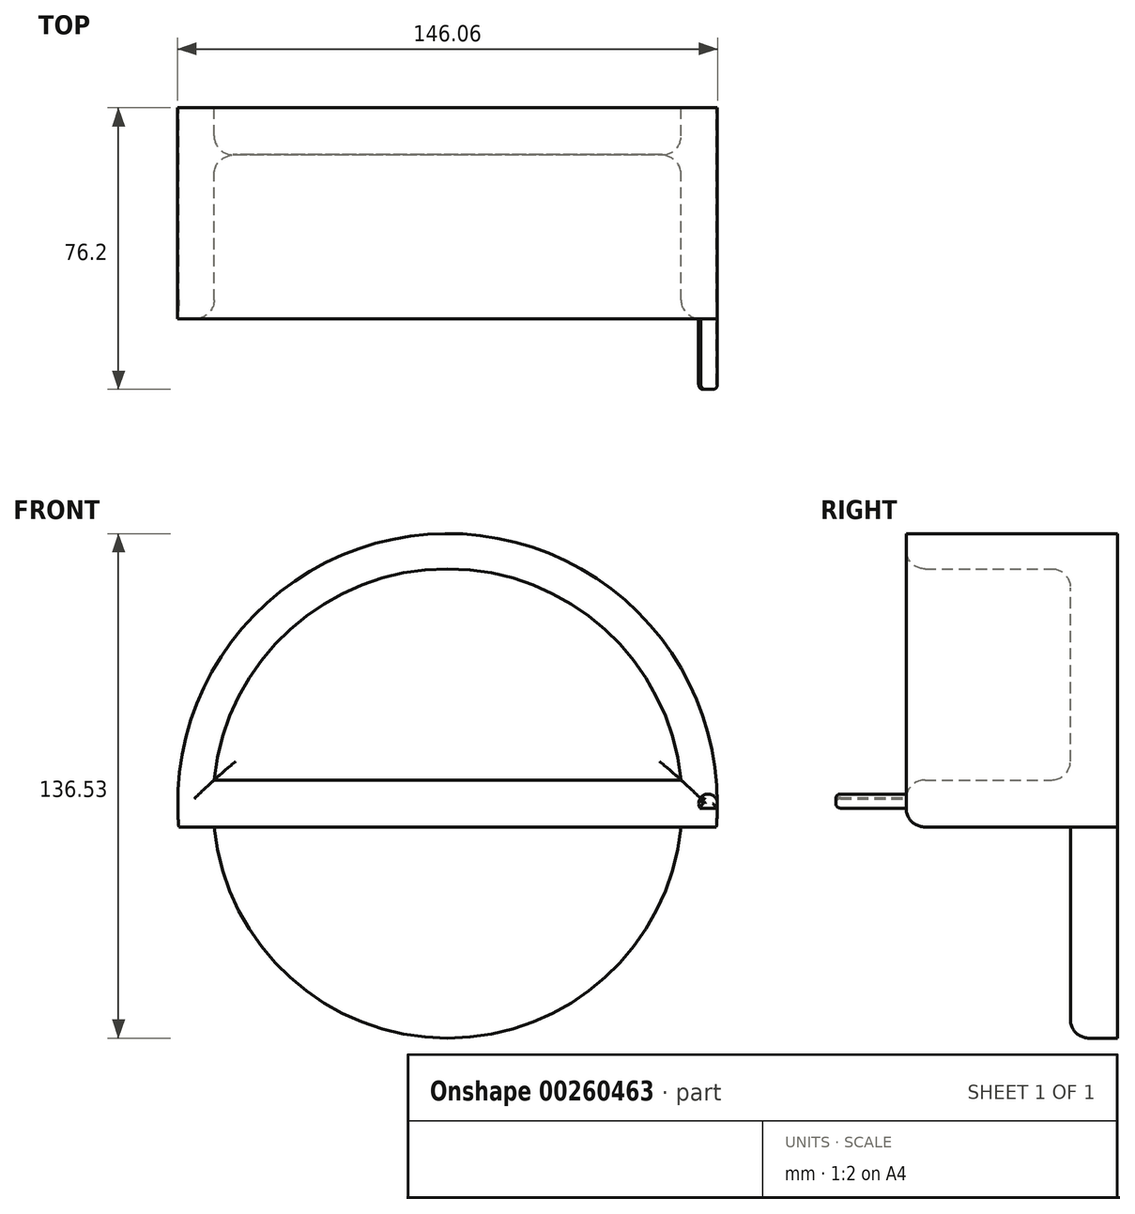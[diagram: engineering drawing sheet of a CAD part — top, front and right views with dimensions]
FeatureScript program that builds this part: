
annotation { "Feature Type Name" : "Feature", "Feature Type Description" : "" }
export const myFeature = defineFeature(function(context is Context, id is Id, definition is map)
    precondition{}
    {
        {
            var Q0;
            Q0=qCreatedBy(makeId("Front.planeOp"),FACE);
            var sketch = newSketch(context, id + "F0", { "sketchPlane" : qUnion([Q0])});
            skCircle(sketch, "E0", {"center": v(0, 0) * mm, "radius": 73.03 * mm});
            skLineSegment(sketch, "E1", {"start": v(-72.75, 6.35) * mm, "end": v(72.75, 6.35) * mm});
            skLineSegment(sketch, "E2", {"start": v(72.75, -6.35) * mm, "end": v(-72.75, -6.35) * mm});
            skCircle(sketch, "E3", {"center": v(0, 0) * mm, "radius": 63.5 * mm});
            skSolve(sketch);
        }
        {
            var Q0;
            {var subQ0=sQuery(id+"F0.wireOp",EDGE,"E1");var subQ1=sQuery(id+"F0.wireOp",EDGE,"E0");var subQ2=makeQuery(id+"F0.imprint","INTERSECT",VERTEX,{"disambiguationData":[OD(0.0)],"derivedFrom":[subQ1,subQ0]});Q0=makeQuery(id+"F0.imprint","IMPRINT",FACE,{"disambiguationData":[TD([[makeQuery(id+"F0.imprint","IMPRINT",EDGE,{"disambiguationData":[TD([[subQ2,1.0]])],"derivedFrom":subQ1}),1.0]])]});}
            var Q1;
            {var subQ0=sQuery(id+"F0.wireOp",EDGE,"E1");var subQ1=sQuery(id+"F0.wireOp",EDGE,"E0");var subQ2=makeQuery(id+"F0.imprint","INTERSECT",VERTEX,{"disambiguationData":[OD(0.0)],"derivedFrom":[subQ1,subQ0]});Q1=makeQuery(id+"F0.imprint","IMPRINT",FACE,{"disambiguationData":[TD([[makeQuery(id+"F0.imprint","IMPRINT",EDGE,{"disambiguationData":[TD([[subQ2,-1.0]])],"derivedFrom":subQ1}),1.0]])]});}
            var Q2;
            {var subQ0=sQuery(id+"F0.wireOp",EDGE,"E2");var subQ1=sQuery(id+"F0.wireOp",EDGE,"E0");var subQ2=makeQuery(id+"F0.imprint","INTERSECT",VERTEX,{"disambiguationData":[OD(0.0)],"derivedFrom":[subQ1,subQ0]});Q2=makeQuery(id+"F0.imprint","IMPRINT",FACE,{"disambiguationData":[TD([[makeQuery(id+"F0.imprint","IMPRINT",EDGE,{"disambiguationData":[TD([[subQ2,1.0]])],"derivedFrom":subQ1}),1.0]])]});}
            var Q3;
            {var subQ0=sQuery(id+"F0.wireOp",EDGE,"E3");var subQ1=sQuery(id+"F0.wireOp",EDGE,"E1");var subQ2=makeQuery(id+"F0.imprint","INTERSECT",VERTEX,{"disambiguationData":[OD(0.0)],"derivedFrom":[subQ1,subQ0]});Q3=makeQuery(id+"F0.imprint","IMPRINT",FACE,{"disambiguationData":[TD([[makeQuery(id+"F0.imprint","IMPRINT",EDGE,{"disambiguationData":[TD([[subQ2,-1.0]])],"derivedFrom":subQ1}),-1.0]])]});}
            var Q4;
            {var subQ0=sQuery(id+"F0.wireOp",EDGE,"E1");var subQ1=sQuery(id+"F0.wireOp",EDGE,"E0");var subQ2=makeQuery(id+"F0.imprint","INTERSECT",VERTEX,{"disambiguationData":[OD(1.0)],"derivedFrom":[subQ1,subQ0]});Q4=makeQuery(id+"F0.imprint","IMPRINT",FACE,{"disambiguationData":[TD([[makeQuery(id+"F0.imprint","IMPRINT",EDGE,{"disambiguationData":[TD([[subQ2,1.0]])],"derivedFrom":subQ1}),1.0]])]});}
            extrude(context, id + "F1", {"entities" : qUnion([Q0, Q1, Q2, Q3, Q4]), "depth" : 57.15 * mm});
        }
        {
            var Q0;
            {var subQ0=sQuery(id+"F0.wireOp",EDGE,"E3");var subQ1=sQuery(id+"F0.wireOp",EDGE,"E1");var subQ2=makeQuery(id+"F0.imprint","INTERSECT",VERTEX,{"disambiguationData":[OD(0.0)],"derivedFrom":[subQ1,subQ0]});Q0=makeQuery(id+"F0.imprint","IMPRINT",FACE,{"disambiguationData":[TD([[makeQuery(id+"F0.imprint","IMPRINT",EDGE,{"disambiguationData":[TD([[subQ2,-1.0]])],"derivedFrom":subQ1}),1.0]])]});}
            var Q1;
            {var subQ0=sQuery(id+"F0.wireOp",EDGE,"E3");var subQ1=sQuery(id+"F0.wireOp",EDGE,"E2");var subQ2=makeQuery(id+"F0.imprint","INTERSECT",VERTEX,{"disambiguationData":[OD(0.0)],"derivedFrom":[subQ1,subQ0]});Q1=makeQuery(id+"F0.imprint","IMPRINT",FACE,{"disambiguationData":[TD([[makeQuery(id+"F0.imprint","IMPRINT",EDGE,{"disambiguationData":[TD([[subQ2,-1.0]])],"derivedFrom":subQ1}),1.0]])]});}
            extrude(context, id + "F2", {"entities" : qUnion([Q0, Q1]), "operationType" : NewBodyOperationType.ADD, "depth" : 12.7 * mm});
        }
        {
            var Q0;
            Q0=makeQuery(id+"F2.opExtrude","CAP_EDGE",EDGE,{"disambiguationData":[OSD([sQuery(id+"F0.wireOp",EDGE,"E2")])],"isStart":false});
            var Q1;
            {var subQ0=sQuery(id+"F0.wireOp",EDGE,"E3");var subQ1=sQuery(id+"F0.wireOp",EDGE,"E2");Q1=makeQuery(id+"F2.opExtrude","CAP_EDGE",EDGE,{"disambiguationData":[OSD([subQ0]),TDD([makeQuery(id+"F0.imprint","IMPRINT",EDGE,{"disambiguationData":[TD([[makeQuery(id+"F0.imprint","INTERSECT",VERTEX,{"disambiguationData":[OD(0.0)],"derivedFrom":[subQ1,subQ0]}),1.0]])],"derivedFrom":subQ0})])],"isStart":false});}
            var Q2;
            Q2=makeQuery(id+"F2.opExtrude","CAP_FACE",FACE,{"disambiguationData":[OSD([sQuery(id+"F0.wireOp",EDGE,"E1"),sQuery(id+"F0.wireOp",EDGE,"E3")])],"isStart":false});
            var Q3;
            {var subQ0=sQuery(id+"F0.wireOp",EDGE,"E3");var subQ1=sQuery(id+"F0.wireOp",EDGE,"E2");Q3=makeQuery(id+"F1.opExtrude","CAP_EDGE",EDGE,{"disambiguationData":[OSD([subQ0]),TDD([makeQuery(id+"F0.imprint","IMPRINT",EDGE,{"disambiguationData":[TD([[makeQuery(id+"F0.imprint","INTERSECT",VERTEX,{"disambiguationData":[OD(0.0)],"derivedFrom":[subQ1,subQ0]}),1.0]])],"derivedFrom":subQ0})])],"isStart":false});}
            var Q4;
            {var subQ0=sQuery(id+"F0.wireOp",EDGE,"E3");var subQ1=sQuery(id+"F0.wireOp",EDGE,"E1");Q4=makeQuery(id+"F1.opExtrude","CAP_EDGE",EDGE,{"disambiguationData":[OSD([subQ0]),TDD([makeQuery(id+"F0.imprint","IMPRINT",EDGE,{"disambiguationData":[TD([[makeQuery(id+"F0.imprint","INTERSECT",VERTEX,{"disambiguationData":[OD(0.0)],"derivedFrom":[subQ1,subQ0]}),1.0]])],"derivedFrom":subQ0})])],"isStart":false});}
            var Q5;
            Q5=makeQuery(id+"F1.opExtrude","CAP_EDGE",EDGE,{"disambiguationData":[OSD([sQuery(id+"F0.wireOp",EDGE,"E1")])],"isStart":false});
            var Q6;
            Q6=makeQuery(id+"F1.opExtrude","CAP_EDGE",EDGE,{"disambiguationData":[OSD([sQuery(id+"F0.wireOp",EDGE,"E2")])],"isStart":false});
            fillet(context, id + "F3", {"entities" : qUnion([Q0, Q1, Q2, Q3, Q4, Q5, Q6]), "radius" : 5.08 * mm, "tangentPropagation" : true, "allowEdgeOverflow" : false});
        }
        {
            var Q0;
            Q0=makeQuery(id+"F1.opExtrude","CAP_FACE",FACE,{"disambiguationData":[OSD([sQuery(id+"F0.wireOp",EDGE,"E0"),sQuery(id+"F0.wireOp",EDGE,"E1"),sQuery(id+"F0.wireOp",EDGE,"E2"),sQuery(id+"F0.wireOp",EDGE,"E3")])],"isStart":false});
            var sketch = newSketch(context, id + "F4", { "sketchPlane" : qUnion([Q0])});
            skPoint(sketch, "E4", {"position": v(73.03, 0) * mm});
            skLineSegment(sketch, "E5", {"start": v(73.03, 0) * mm, "end": v(70.48, 0) * mm});
            skCircle(sketch, "E6", {"center": v(70.48, 0) * mm, "radius": 2.54 * mm});
            skSolve(sketch);
        }
        {
            var Q0;
            {var subQ3=sQuery(id+"F0.wireOp",EDGE,"E0");var subQ8=sQuery(id+"F4.wireOp",EDGE,"E6");var subQ10=makeQuery(id+"F4.imprint","INTERSECT",VERTEX,{"derivedFrom":[makeQuery(id+"F1.opExtrude","CAP_EDGE",EDGE,{"disambiguationData":[OSD([subQ3])],"isStart":false}),subQ8]});Q0=makeQuery(id+"F4.imprint","IMPRINT",FACE,{"disambiguationData":[TD([[makeQuery(id+"F4.imprint","IMPRINT",EDGE,{"disambiguationData":[TD([[subQ10,-1.0]])],"derivedFrom":subQ8}),1.0]])]});}
            extrude(context, id + "F5", {"entities" : qUnion([Q0]), "operationType" : NewBodyOperationType.ADD, "depth" : 19.05 * mm});
        }
        {
            var Q0;
            Q0=makeQuery(id+"F5.opExtrude","CAP_FACE",FACE,{"disambiguationData":[OSD([sQuery(id+"F0.wireOp",EDGE,"E0"),sQuery(id+"F0.wireOp",EDGE,"E1"),sQuery(id+"F0.wireOp",EDGE,"E2"),sQuery(id+"F0.wireOp",EDGE,"E3"),sQuery(id+"F4.wireOp",EDGE,"E6")])],"isStart":false});
            fillet(context, id + "F6", {"entities" : qUnion([Q0]), "radius" : 1.27 * mm, "tangentPropagation" : true, "allowEdgeOverflow" : false});
        }
    });
